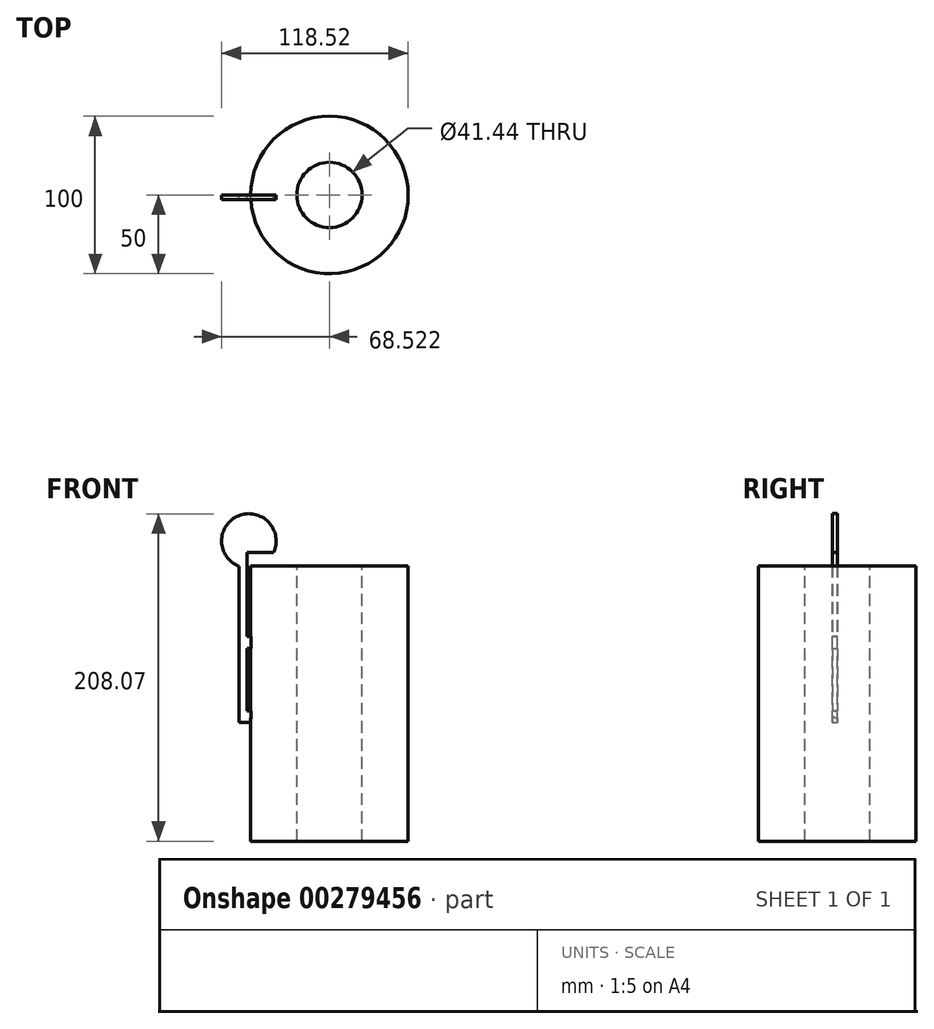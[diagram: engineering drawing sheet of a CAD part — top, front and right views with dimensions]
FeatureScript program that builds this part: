
annotation { "Feature Type Name" : "Feature", "Feature Type Description" : "" }
export const myFeature = defineFeature(function(context is Context, id is Id, definition is map)
    precondition{}
    {
        {
            var Q0;
            Q0=qCreatedBy(makeId("Front.planeOp"),FACE);
            var sketch = newSketch(context, id + "F0", { "sketchPlane" : qUnion([Q0])});
            skLineSegment(sketch, "E0.bottom", {"start": v(-23.46, 120.42) * mm, "end": v(26.54, 120.42) * mm});
            skLineSegment(sketch, "E0.top", {"start": v(-23.46, -54.58) * mm, "end": v(26.54, -54.58) * mm});
            skLineSegment(sketch, "E0.left", {"start": v(-23.46, 120.42) * mm, "end": v(-23.46, -54.58) * mm});
            skLineSegment(sketch, "E0.right", {"start": v(26.54, 120.42) * mm, "end": v(26.54, -54.58) * mm});
            skSolve(sketch);
        }
        {
            var Q0;
            Q0=makeQuery(id+"F0.imprint","IMPRINT",FACE,{"disambiguationData":[TD([[makeQuery(id+"F0.imprint","IMPRINT",EDGE,{"derivedFrom":sQuery(id+"F0.wireOp",EDGE,"E0.bottom")}),-1.0]])]});
            var Q1;
            Q1=sQuery(id+"F0.wireOp",EDGE,"E0.right");
            revolve(context, id + "F1", {"entities" : qUnion([Q0]), "axis" : qUnion([Q1]), "revolveType" : RevolveType.FULL});
        }
        {
            var Q0;
            Q0=makeQuery(id+"F1.opRevolve","SWEPT_FACE",FACE,{"disambiguationData":[OSD([sQuery(id+"F0.wireOp",EDGE,"E0.bottom")])]});
            var sketch = newSketch(context, id + "F2", { "sketchPlane" : qUnion([Q0])});
            skCircle(sketch, "E1", {"center": v(26.54, 0) * mm, "radius": 20.72 * mm});
            skSolve(sketch);
        }
        {
            var Q0;
            Q0=makeQuery(id+"F2.imprint","IMPRINT",FACE,{"disambiguationData":[TD([[makeQuery(id+"F2.imprint","IMPRINT",EDGE,{"derivedFrom":sQuery(id+"F2.wireOp",EDGE,"E1")}),1.0]])]});
            extrude(context, id + "F3", {"entities" : qUnion([Q0]), "operationType" : NewBodyOperationType.REMOVE, "oppositeDirection" : true, "depth" : 235 * mm});
        }
        {
            var Q0;
            Q0=qCreatedBy(makeId("Front.planeOp"),FACE);
            var sketch = newSketch(context, id + "F4", { "sketchPlane" : qUnion([Q0])});
            skLineSegment(sketch, "E2", {"start": v(-23.66, 20.86) * mm, "end": v(-30.85, 20.86) * mm});
            skLineSegment(sketch, "E3", {"start": v(-30.85, 20.86) * mm, "end": v(-30.85, 119.99) * mm});
            skArc(sketch, "E4", {"start": v(-8.93, 128.9) * mm, "mid": v(-31.17, 152.22) * mm, "end": v(-30.85, 119.99) * mm});
            skLineSegment(sketch, "E5", {"start": v(-8.93, 128.9) * mm, "end": v(-25.82, 128.9) * mm});
            skLineSegment(sketch, "E6", {"start": v(-25.82, 128.9) * mm, "end": v(-25.82, 75.64) * mm});
            skLineSegment(sketch, "E7", {"start": v(-25.82, 75.64) * mm, "end": v(-23.13, 75.64) * mm});
            skLineSegment(sketch, "E8", {"start": v(-23.13, 75.64) * mm, "end": v(-23.13, 67.95) * mm});
            skLineSegment(sketch, "E9", {"start": v(-23.13, 67.95) * mm, "end": v(-25.82, 67.95) * mm});
            skLineSegment(sketch, "E10", {"start": v(-25.82, 67.95) * mm, "end": v(-25.82, 28.35) * mm});
            skLineSegment(sketch, "E11", {"start": v(-25.82, 28.35) * mm, "end": v(-23.13, 28.35) * mm});
            skLineSegment(sketch, "E12", {"start": v(-23.13, 28.35) * mm, "end": v(-23.66, 20.86) * mm});
            skSolve(sketch);
        }
        {
            var Q0;
            Q0=makeQuery(id+"F4.imprint","IMPRINT",FACE,{"disambiguationData":[TD([[makeQuery(id+"F4.imprint","IMPRINT",EDGE,{"derivedFrom":sQuery(id+"F4.wireOp",EDGE,"E2")}),-1.0]])]});
            var Q1;
            Q1=sQuery(id+"F4.wireOp",EDGE,"E3");
            var Q2;
            Q2=sQuery(id+"F4.wireOp",EDGE,"E2");
            var Q3;
            Q3=sQuery(id+"F4.wireOp",EDGE,"E12");
            var Q4;
            Q4=sQuery(id+"F4.wireOp",EDGE,"E5");
            var Q5;
            Q5=sQuery(id+"F4.wireOp",EDGE,"E6");
            var Q6;
            Q6=sQuery(id+"F4.wireOp",EDGE,"E10");
            var Q7;
            Q7=sQuery(id+"F4.wireOp",EDGE,"E8");
            var Q8;
            Q8=sQuery(id+"F4.wireOp",EDGE,"E11");
            var Q9;
            Q9=sQuery(id+"F4.wireOp",EDGE,"E7");
            var Q10;
            Q10=sQuery(id+"F4.wireOp",EDGE,"E9");
            var Q11;
            Q11=sQuery(id+"F4.wireOp",EDGE,"E4");
            extrude(context, id + "F5", {"entities" : qUnion([Q0]), "operationType" : NewBodyOperationType.ADD, "surfaceEntities" : qUnion([Q1, Q2, Q3, Q4, Q5, Q6, Q7, Q8, Q9, Q10, Q11]), "depth" : 3 * mm});
        }
    });
